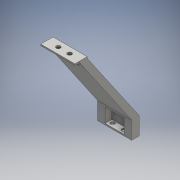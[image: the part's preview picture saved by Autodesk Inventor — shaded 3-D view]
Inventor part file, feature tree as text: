
AUTODESK INVENTOR PART (.ipt)
format: ipt  version: 2016 (Build 200138000, 138)  size: 173,056 bytes
history: native  units: mm
features: sketch x6, extrude x4, hole x2
ambient origin geometry x8: Origin, YZ Plane, XZ Plane, XY Plane, X Axis, Y Axis, Z Axis, Center Point
bodies: Solid1 (feature_tree)
feature tree (12):
  extrude  "Extrusion1"  Depth=1.5mm
  extrude  "Extrusion2"  Depth=55.0mm
  hole  "Hole1"  [1 undecoded]
  hole  "Hole2"  [1 undecoded]
  extrude  "Extrusion3"  Depth=8.0mm
  extrude  "Extrusion4"  Depth=20.0mm
  sketch  "Sketch1"  dims[d4=13.0mm d5=1.5mm]
  sketch  "Sketch2"  dims[d6=80.0mm d7=55.0mm]
  sketch  "Sketch3"  dims[d8=18.5mm d9=8.0mm]
  sketch  "Sketch5"  dims[d10=1.5mm d11=5.0mm]
  sketch  "Sketch6"  dims[d12=36.0mm d13=0.0mm d14=8.0mm]
  sketch  "Sketch7"  dims[d15=1.5mm d16=20.0mm d17=15.0mm d18=7.0mm d19=0.0mm d20=4.0mm d21=4.35mm d22=4.35mm d23=6.0mm d24=6.0mm d25=4.35mm d26=6.0mm d27=4.0mm d28=2.0mm d29=90.0deg d30=8.0mm d31=20.594885mm d35=13.0mm d36=4.35mm d37=6.0mm d38=4.35mm d39=6.0mm d40=4.35mm d41=6.0mm d42=4.0mm d43=2.0mm d44=90.0deg d45=8.0mm d46=20.594885mm d47=6.0mm d48=6.0mm d49=8.0mm d50=24.0mm d51=90.0deg d52=7.0mm d53=0.0mm d54=24.0mm d55=12.0mm d56=0.0mm]
note: 2 required parameter values undecoded (feature->parameter linkage not recoverable at this tier; creation-order binding heuristic only, values carry confidence <= 0.55)
